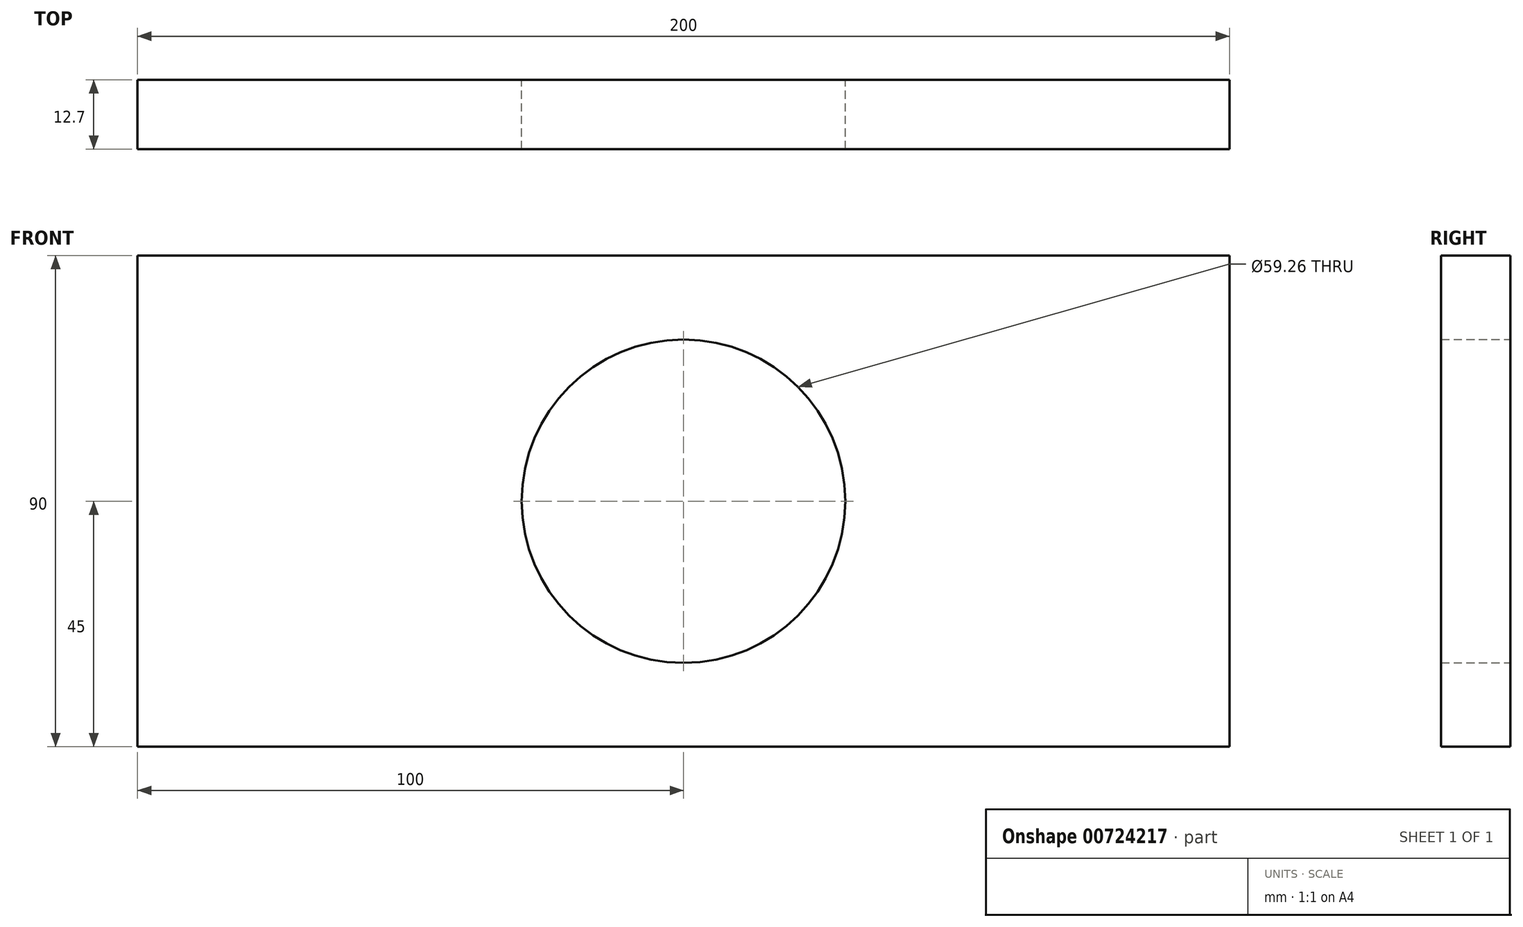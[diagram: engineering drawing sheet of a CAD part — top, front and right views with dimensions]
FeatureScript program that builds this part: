
annotation { "Feature Type Name" : "Feature", "Feature Type Description" : "" }
export const myFeature = defineFeature(function(context is Context, id is Id, definition is map)
    precondition{}
    {
        {
            var Q0;
            Q0=qCreatedBy(makeId("Front.planeOp"),FACE);
            var sketch = newSketch(context, id + "F0", { "sketchPlane" : qUnion([Q0])});
            skLineSegment(sketch, "E0.bottom", {"start": v(100, -45) * mm, "end": v(-100, -45) * mm});
            skLineSegment(sketch, "E0.top", {"start": v(100, 45) * mm, "end": v(-100, 45) * mm});
            skLineSegment(sketch, "E0.left", {"start": v(100, -45) * mm, "end": v(100, 45) * mm});
            skLineSegment(sketch, "E0.right", {"start": v(-100, -45) * mm, "end": v(-100, 45) * mm});
            skPoint(sketch, "E0.middle", {"position": v(0, 0) * mm});
            skCircle(sketch, "E1", {"center": v(0, 0) * mm, "radius": 29.63 * mm});
            skSolve(sketch);
        }
        {
            var Q0;
            Q0=makeQuery(id+"F0.imprint","IMPRINT",FACE,{"disambiguationData":[TD([[makeQuery(id+"F0.imprint","IMPRINT",EDGE,{"derivedFrom":sQuery(id+"F0.wireOp",EDGE,"E0.bottom")}),-1.0]])]});
            extrude(context, id + "F1", {"entities" : qUnion([Q0]), "depth" : 38.1 * mm, "offsetDistance" : 25.4 * mm});
        }
        {
            var Q0;
            Q0 = qSketchRegion(id + "FajILLZd46BhbX3_1", true);
            var Q1;
            Q1=makeQuery(id+"F1.opExtrude","CAP_FACE",FACE,{"disambiguationData":[OSD([sQuery(id+"F0.wireOp",EDGE,"E0.bottom"),sQuery(id+"F0.wireOp",EDGE,"E0.top"),sQuery(id+"F0.wireOp",EDGE,"E0.left"),sQuery(id+"F0.wireOp",EDGE,"E0.right"),sQuery(id+"F0.wireOp",EDGE,"E1")])],"isStart":false});
            extrude(context, id + "F2", {"entities" : qUnion([Q0, Q1]), "operationType" : NewBodyOperationType.REMOVE, "oppositeDirection" : true, "depth" : 25.4 * mm, "offsetDistance" : 25.4 * mm});
        }
    });
